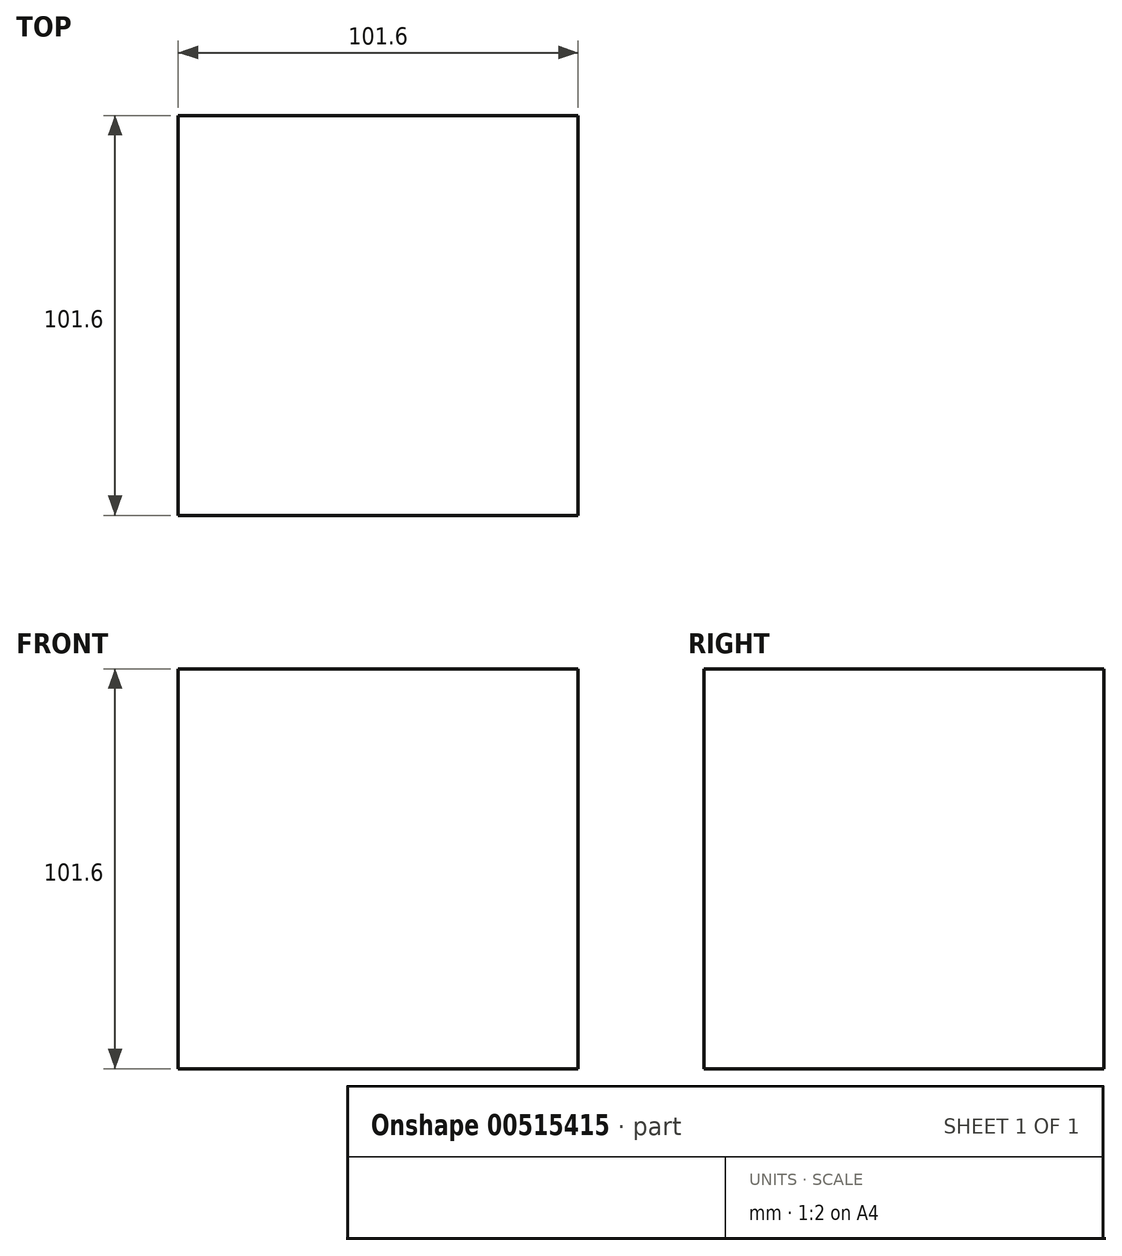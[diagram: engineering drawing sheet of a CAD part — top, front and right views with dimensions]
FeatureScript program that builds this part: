
annotation { "Feature Type Name" : "Feature", "Feature Type Description" : "" }
export const myFeature = defineFeature(function(context is Context, id is Id, definition is map)
    precondition{}
    {
        {
            var Q0;
            Q0=qCreatedBy(makeId("Top.planeOp"),FACE);
            var sketch = newSketch(context, id + "F0", { "sketchPlane" : qUnion([Q0])});
            skLineSegment(sketch, "E0.bottom", {"start": v(-50.7, 38.3) * mm, "end": v(50.9, 38.3) * mm});
            skLineSegment(sketch, "E0.top", {"start": v(-50.7, -63.3) * mm, "end": v(50.9, -63.3) * mm});
            skLineSegment(sketch, "E0.left", {"start": v(-50.7, 38.3) * mm, "end": v(-50.7, -63.3) * mm});
            skLineSegment(sketch, "E0.right", {"start": v(50.9, 38.3) * mm, "end": v(50.9, -63.3) * mm});
            skSolve(sketch);
        }
        {
            var Q0;
            Q0 = qSketchRegion(id + "F0", true);
            extrude(context, id + "F1", {"entities" : qUnion([Q0]), "depth" : 101.6 * mm, "offsetDistance" : 25.4 * mm});
        }
    });
